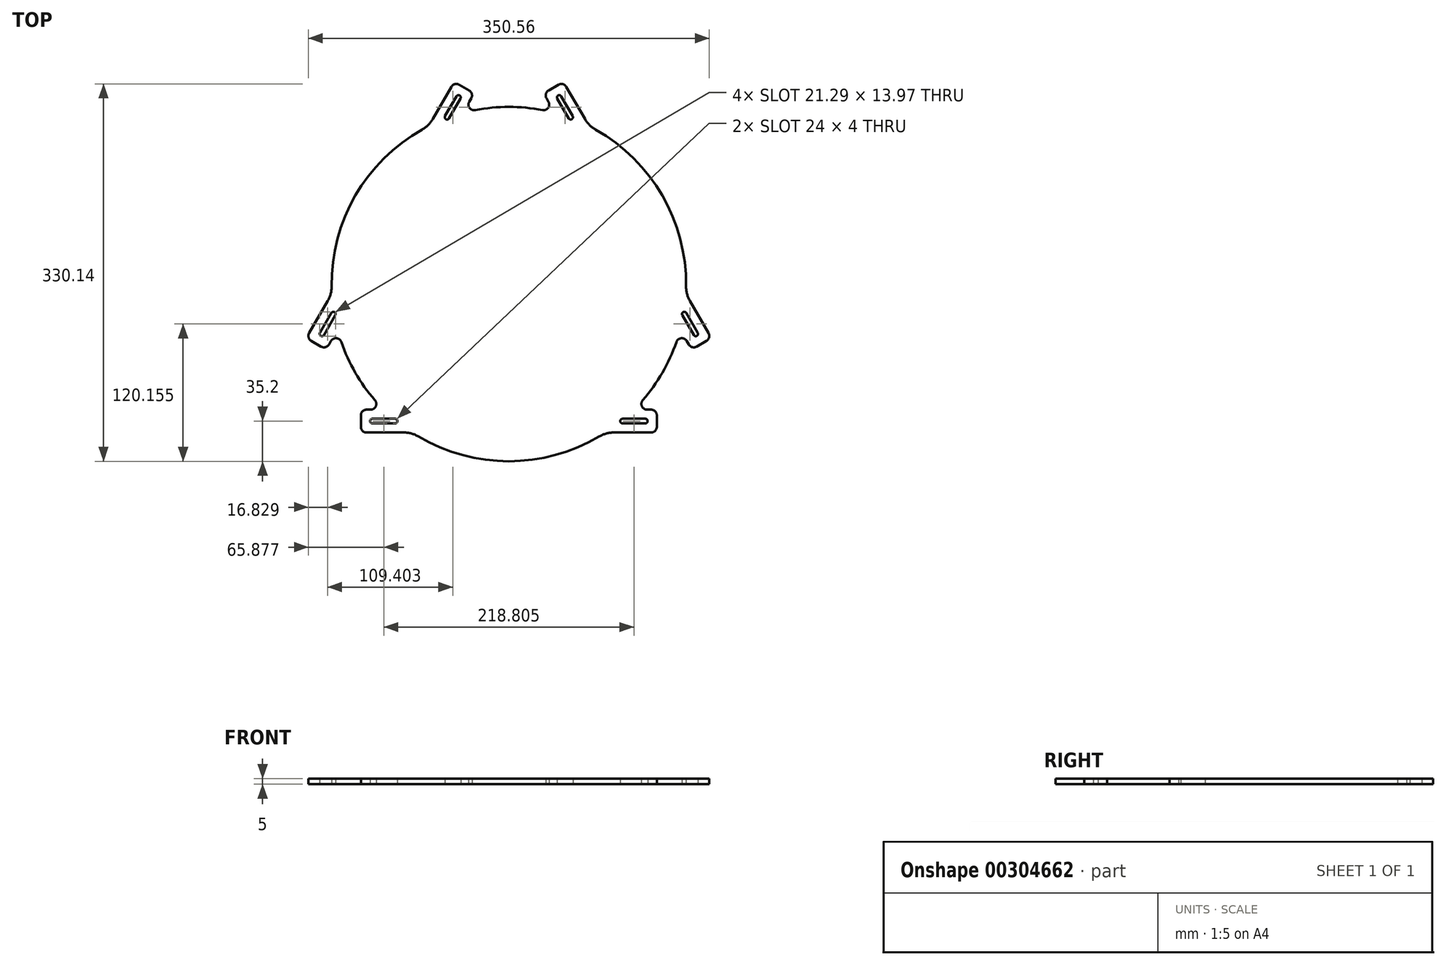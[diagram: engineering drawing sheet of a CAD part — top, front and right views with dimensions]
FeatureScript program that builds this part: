
annotation { "Feature Type Name" : "Feature", "Feature Type Description" : "" }
export const myFeature = defineFeature(function(context is Context, id is Id, definition is map)
    precondition{}
    {
        {
            var Q0;
            Q0=qCreatedBy(makeId("Top.planeOp"),FACE);
            var sketch = newSketch(context, id + "F0", { "sketchPlane" : qUnion([Q0])});
            skCircle(sketch, "E0", {"center": v(0, 0) * mm, "radius": 155 * mm});
            skCircle(sketch, "E1", {"center": v(0, 0) * mm, "radius": 150 * mm, "construction": true});
            skLineSegment(sketch, "E2.0", {"start": v(8.66, 244.6) * mm, "end": v(216.16, -114.8) * mm, "construction": true});
            skLineSegment(sketch, "E3.0", {"start": v(-216.16, -114.8) * mm, "end": v(-8.66, 244.6) * mm, "construction": true});
            skLineSegment(sketch, "E4.0", {"start": v(207.5, -129.8) * mm, "end": v(-207.5, -129.8) * mm, "construction": true});
            skLineSegment(sketch, "E5.0", {"start": v(207.5, -109.8) * mm, "end": v(-207.5, -109.8) * mm, "construction": true});
            skLineSegment(sketch, "E6.0", {"start": v(-198.84, -124.8) * mm, "end": v(8.66, 234.6) * mm, "construction": true});
            skLineSegment(sketch, "E7.0", {"start": v(-8.66, 234.6) * mm, "end": v(198.84, -124.8) * mm, "construction": true});
            skLineSegment(sketch, "E8", {"start": v(-40.39, 149.65) * mm, "end": v(-30.39, 166.97) * mm});
            skLineSegment(sketch, "E9", {"start": v(40.39, 149.65) * mm, "end": v(30.39, 166.97) * mm});
            skLineSegment(sketch, "E10", {"start": v(-149.8, -39.85) * mm, "end": v(-159.8, -57.17) * mm});
            skLineSegment(sketch, "E11", {"start": v(-109.4, -109.8) * mm, "end": v(-129.4, -109.8) * mm});
            skLineSegment(sketch, "E12", {"start": v(109.4, -109.8) * mm, "end": v(129.4, -109.8) * mm});
            skLineSegment(sketch, "E13", {"start": v(149.8, -39.85) * mm, "end": v(159.8, -57.17) * mm});
            skLineSegment(sketch, "E14", {"start": v(-30.39, 166.97) * mm, "end": v(-47.7, 176.97) * mm});
            skLineSegment(sketch, "E15", {"start": v(-47.7, 176.97) * mm, "end": v(-70.05, 138.27) * mm});
            skLineSegment(sketch, "E16", {"start": v(30.39, 166.97) * mm, "end": v(47.7, 176.97) * mm});
            skLineSegment(sketch, "E17", {"start": v(47.7, 176.97) * mm, "end": v(70.05, 138.27) * mm});
            skLineSegment(sketch, "E18", {"start": v(-159.8, -57.17) * mm, "end": v(-177.11, -47.17) * mm});
            skLineSegment(sketch, "E19", {"start": v(-177.11, -47.17) * mm, "end": v(-154.77, -8.47) * mm});
            skLineSegment(sketch, "E20", {"start": v(-129.4, -109.8) * mm, "end": v(-129.4, -129.8) * mm});
            skLineSegment(sketch, "E21", {"start": v(-129.4, -129.8) * mm, "end": v(-84.72, -129.8) * mm});
            skLineSegment(sketch, "E22", {"start": v(129.4, -109.8) * mm, "end": v(129.4, -129.8) * mm});
            skLineSegment(sketch, "E23", {"start": v(129.4, -129.8) * mm, "end": v(84.72, -129.8) * mm});
            skLineSegment(sketch, "E24", {"start": v(159.8, -57.17) * mm, "end": v(177.11, -47.17) * mm});
            skLineSegment(sketch, "E25", {"start": v(177.11, -47.17) * mm, "end": v(154.77, -8.47) * mm});
            skPoint(sketch, "E26", {"position": v(-39.05, 171.97) * mm});
            skPoint(sketch, "E27", {"position": v(39.05, 171.97) * mm});
            skPoint(sketch, "E28", {"position": v(-168.45, -52.17) * mm});
            skPoint(sketch, "E29", {"position": v(-129.4, -119.8) * mm});
            skPoint(sketch, "E30", {"position": v(129.4, -119.8) * mm});
            skPoint(sketch, "E31", {"position": v(168.45, -52.17) * mm});
            skLineSegment(sketch, "E32", {"start": v(-39.05, 171.97) * mm, "end": v(-44.05, 163.3) * mm, "construction": true});
            skLineSegment(sketch, "E33", {"start": v(-44.05, 163.3) * mm, "end": v(-54.05, 145.99) * mm, "construction": true});
            skLineSegment(sketch, "E34", {"start": v(39.05, 171.97) * mm, "end": v(44.05, 163.3) * mm, "construction": true});
            skLineSegment(sketch, "E35", {"start": v(44.05, 163.3) * mm, "end": v(54.05, 145.99) * mm, "construction": true});
            skLineSegment(sketch, "E36", {"start": v(-168.45, -52.17) * mm, "end": v(-163.45, -43.5) * mm, "construction": true});
            skLineSegment(sketch, "E37", {"start": v(-163.45, -43.5) * mm, "end": v(-153.45, -26.19) * mm, "construction": true});
            skLineSegment(sketch, "E38", {"start": v(-129.4, -119.8) * mm, "end": v(-119.4, -119.8) * mm, "construction": true});
            skLineSegment(sketch, "E39", {"start": v(-119.4, -119.8) * mm, "end": v(-99.4, -119.8) * mm, "construction": true});
            skLineSegment(sketch, "E40", {"start": v(129.4, -119.8) * mm, "end": v(119.4, -119.8) * mm, "construction": true});
            skLineSegment(sketch, "E41", {"start": v(119.4, -119.8) * mm, "end": v(99.4, -119.8) * mm, "construction": true});
            skLineSegment(sketch, "E42", {"start": v(168.45, -52.17) * mm, "end": v(163.45, -43.5) * mm, "construction": true});
            skLineSegment(sketch, "E43", {"start": v(163.45, -43.5) * mm, "end": v(153.45, -26.19) * mm, "construction": true});
            skCircle(sketch, "E44", {"center": v(-44.05, 163.3) * mm, "radius": 2 * mm});
            skCircle(sketch, "E45", {"center": v(-54.05, 145.99) * mm, "radius": 2 * mm});
            skCircle(sketch, "E46", {"center": v(54.05, 145.99) * mm, "radius": 2 * mm});
            skCircle(sketch, "E47", {"center": v(44.05, 163.3) * mm, "radius": 2 * mm});
            skCircle(sketch, "E48", {"center": v(-163.45, -43.5) * mm, "radius": 2 * mm});
            skCircle(sketch, "E49", {"center": v(-153.45, -26.19) * mm, "radius": 2 * mm});
            skCircle(sketch, "E50", {"center": v(-99.4, -119.8) * mm, "radius": 2 * mm});
            skCircle(sketch, "E51", {"center": v(-119.4, -119.8) * mm, "radius": 2 * mm});
            skCircle(sketch, "E52", {"center": v(99.4, -119.8) * mm, "radius": 2 * mm});
            skCircle(sketch, "E53", {"center": v(119.4, -119.8) * mm, "radius": 2 * mm});
            skCircle(sketch, "E54", {"center": v(153.45, -26.19) * mm, "radius": 2 * mm});
            skCircle(sketch, "E55", {"center": v(163.45, -43.5) * mm, "radius": 2 * mm});
            skLineSegment(sketch, "E56.0", {"start": v(119.4, -117.8) * mm, "end": v(99.4, -117.8) * mm});
            skLineSegment(sketch, "E57.0", {"start": v(119.4, -121.8) * mm, "end": v(99.4, -121.8) * mm});
            skLineSegment(sketch, "E58.0", {"start": v(161.72, -44.5) * mm, "end": v(151.72, -27.19) * mm});
            skLineSegment(sketch, "E59.0", {"start": v(165.18, -42.5) * mm, "end": v(155.18, -25.19) * mm});
            skLineSegment(sketch, "E60.0", {"start": v(-119.4, -121.8) * mm, "end": v(-99.4, -121.8) * mm});
            skLineSegment(sketch, "E61.0", {"start": v(-119.4, -117.8) * mm, "end": v(-99.4, -117.8) * mm});
            skLineSegment(sketch, "E62.0", {"start": v(-161.72, -44.5) * mm, "end": v(-151.72, -27.19) * mm});
            skLineSegment(sketch, "E63.0", {"start": v(-165.18, -42.5) * mm, "end": v(-155.18, -25.19) * mm});
            skLineSegment(sketch, "E64.0", {"start": v(-42.32, 162.3) * mm, "end": v(-52.32, 144.99) * mm});
            skLineSegment(sketch, "E65.0", {"start": v(-45.78, 164.3) * mm, "end": v(-55.78, 146.99) * mm});
            skLineSegment(sketch, "E66.0", {"start": v(45.78, 164.3) * mm, "end": v(55.78, 146.99) * mm});
            skLineSegment(sketch, "E67.0", {"start": v(42.32, 162.3) * mm, "end": v(52.32, 144.99) * mm});
            skSolve(sketch);
        }
        {
            var Q0;
            Q0=qSketchRegion(id+"F0",true);
            extrude(context, id + "F1", {"entities" : qUnion([Q0]), "depth" : 5 * mm});
        }
        {
            var Q0;
            Q0=makeQuery(id+"F1.opExtrude","SWEPT_EDGE",EDGE,{"disambiguationData":[OSD([sQuery(id+"F0.wireOp",EDGE,"E14"),sQuery(id+"F0.wireOp",EDGE,"E15")])]});
            var Q1;
            Q1=makeQuery(id+"F1.opExtrude","SWEPT_EDGE",EDGE,{"disambiguationData":[OSD([sQuery(id+"F0.wireOp",EDGE,"E8"),sQuery(id+"F0.wireOp",EDGE,"E14")])]});
            var Q2;
            Q2=makeQuery(id+"F1.opExtrude","SWEPT_EDGE",EDGE,{"disambiguationData":[OSD([sQuery(id+"F0.wireOp",EDGE,"E9"),sQuery(id+"F0.wireOp",EDGE,"E16")])]});
            var Q3;
            Q3=makeQuery(id+"F1.opExtrude","SWEPT_EDGE",EDGE,{"disambiguationData":[OSD([sQuery(id+"F0.wireOp",EDGE,"E16"),sQuery(id+"F0.wireOp",EDGE,"E17")])]});
            var Q4;
            Q4=makeQuery(id+"F1.opExtrude","SWEPT_EDGE",EDGE,{"disambiguationData":[OSD([sQuery(id+"F0.wireOp",EDGE,"E24"),sQuery(id+"F0.wireOp",EDGE,"E25")])]});
            var Q5;
            Q5=makeQuery(id+"F1.opExtrude","SWEPT_EDGE",EDGE,{"disambiguationData":[OSD([sQuery(id+"F0.wireOp",EDGE,"E18"),sQuery(id+"F0.wireOp",EDGE,"E19")])]});
            var Q6;
            Q6=makeQuery(id+"F1.opExtrude","SWEPT_EDGE",EDGE,{"disambiguationData":[OSD([sQuery(id+"F0.wireOp",EDGE,"E11"),sQuery(id+"F0.wireOp",EDGE,"E20")])]});
            var Q7;
            Q7=makeQuery(id+"F1.opExtrude","SWEPT_EDGE",EDGE,{"disambiguationData":[OSD([sQuery(id+"F0.wireOp",EDGE,"E12"),sQuery(id+"F0.wireOp",EDGE,"E22")])]});
            var Q8;
            Q8=makeQuery(id+"F1.opExtrude","SWEPT_EDGE",EDGE,{"disambiguationData":[OSD([sQuery(id+"F0.wireOp",EDGE,"E13"),sQuery(id+"F0.wireOp",EDGE,"E24")])]});
            var Q9;
            Q9=makeQuery(id+"F1.opExtrude","SWEPT_EDGE",EDGE,{"disambiguationData":[OSD([sQuery(id+"F0.wireOp",EDGE,"E22"),sQuery(id+"F0.wireOp",EDGE,"E23")])]});
            var Q10;
            Q10=makeQuery(id+"F1.opExtrude","SWEPT_EDGE",EDGE,{"disambiguationData":[OSD([sQuery(id+"F0.wireOp",EDGE,"E20"),sQuery(id+"F0.wireOp",EDGE,"E21")])]});
            var Q11;
            Q11=makeQuery(id+"F1.opExtrude","SWEPT_EDGE",EDGE,{"disambiguationData":[OSD([sQuery(id+"F0.wireOp",EDGE,"E10"),sQuery(id+"F0.wireOp",EDGE,"E18")])]});
            fillet(context, id + "F2", {"entities" : qUnion([Q0, Q1, Q2, Q3, Q4, Q5, Q6, Q7, Q8, Q9, Q10, Q11]), "radius" : 5 * mm, "tangentPropagation" : true, "allowEdgeOverflow" : false});
        }
        {
            var Q0;
            Q0=makeQuery(id+"F1.opExtrude","SWEPT_EDGE",EDGE,{"disambiguationData":[OSD([sQuery(id+"F0.wireOp",EDGE,"E0"),sQuery(id+"F0.wireOp",EDGE,"E10")])]});
            var Q1;
            Q1=makeQuery(id+"F1.opExtrude","SWEPT_EDGE",EDGE,{"disambiguationData":[OSD([sQuery(id+"F0.wireOp",EDGE,"E0"),sQuery(id+"F0.wireOp",EDGE,"E13")])]});
            var Q2;
            Q2=makeQuery(id+"F1.opExtrude","SWEPT_EDGE",EDGE,{"disambiguationData":[OSD([sQuery(id+"F0.wireOp",EDGE,"E0"),sQuery(id+"F0.wireOp",EDGE,"E9")])]});
            var Q3;
            Q3=makeQuery(id+"F1.opExtrude","SWEPT_EDGE",EDGE,{"disambiguationData":[OSD([sQuery(id+"F0.wireOp",EDGE,"E0"),sQuery(id+"F0.wireOp",EDGE,"E8")])]});
            var Q4;
            Q4=makeQuery(id+"F1.opExtrude","SWEPT_EDGE",EDGE,{"disambiguationData":[OSD([sQuery(id+"F0.wireOp",EDGE,"E0"),sQuery(id+"F0.wireOp",EDGE,"E11")])]});
            var Q5;
            Q5=makeQuery(id+"F1.opExtrude","SWEPT_EDGE",EDGE,{"disambiguationData":[OSD([sQuery(id+"F0.wireOp",EDGE,"E0"),sQuery(id+"F0.wireOp",EDGE,"E12")])]});
            fillet(context, id + "F3", {"entities" : qUnion([Q0, Q1, Q2, Q3, Q4, Q5]), "radius" : 5 * mm, "tangentPropagation" : true, "allowEdgeOverflow" : false});
        }
        {
            var Q0;
            Q0=makeQuery(id+"F1.opExtrude","SWEPT_EDGE",EDGE,{"disambiguationData":[OSD([sQuery(id+"F0.wireOp",EDGE,"E0"),sQuery(id+"F0.wireOp",EDGE,"E15")])]});
            var Q1;
            Q1=makeQuery(id+"F1.opExtrude","SWEPT_EDGE",EDGE,{"disambiguationData":[OSD([sQuery(id+"F0.wireOp",EDGE,"E0"),sQuery(id+"F0.wireOp",EDGE,"E19")])]});
            var Q2;
            Q2=makeQuery(id+"F1.opExtrude","SWEPT_EDGE",EDGE,{"disambiguationData":[OSD([sQuery(id+"F0.wireOp",EDGE,"E0"),sQuery(id+"F0.wireOp",EDGE,"E17")])]});
            var Q3;
            Q3=makeQuery(id+"F1.opExtrude","SWEPT_EDGE",EDGE,{"disambiguationData":[OSD([sQuery(id+"F0.wireOp",EDGE,"E0"),sQuery(id+"F0.wireOp",EDGE,"E25")])]});
            var Q4;
            Q4=makeQuery(id+"F1.opExtrude","SWEPT_EDGE",EDGE,{"disambiguationData":[OSD([sQuery(id+"F0.wireOp",EDGE,"E0"),sQuery(id+"F0.wireOp",EDGE,"E21")])]});
            var Q5;
            Q5=makeQuery(id+"F1.opExtrude","SWEPT_EDGE",EDGE,{"disambiguationData":[OSD([sQuery(id+"F0.wireOp",EDGE,"E0"),sQuery(id+"F0.wireOp",EDGE,"E23")])]});
            fillet(context, id + "F4", {"entities" : qUnion([Q0, Q1, Q2, Q3, Q4, Q5]), "radius" : 25 * mm, "tangentPropagation" : true, "allowEdgeOverflow" : false});
        }
    });
